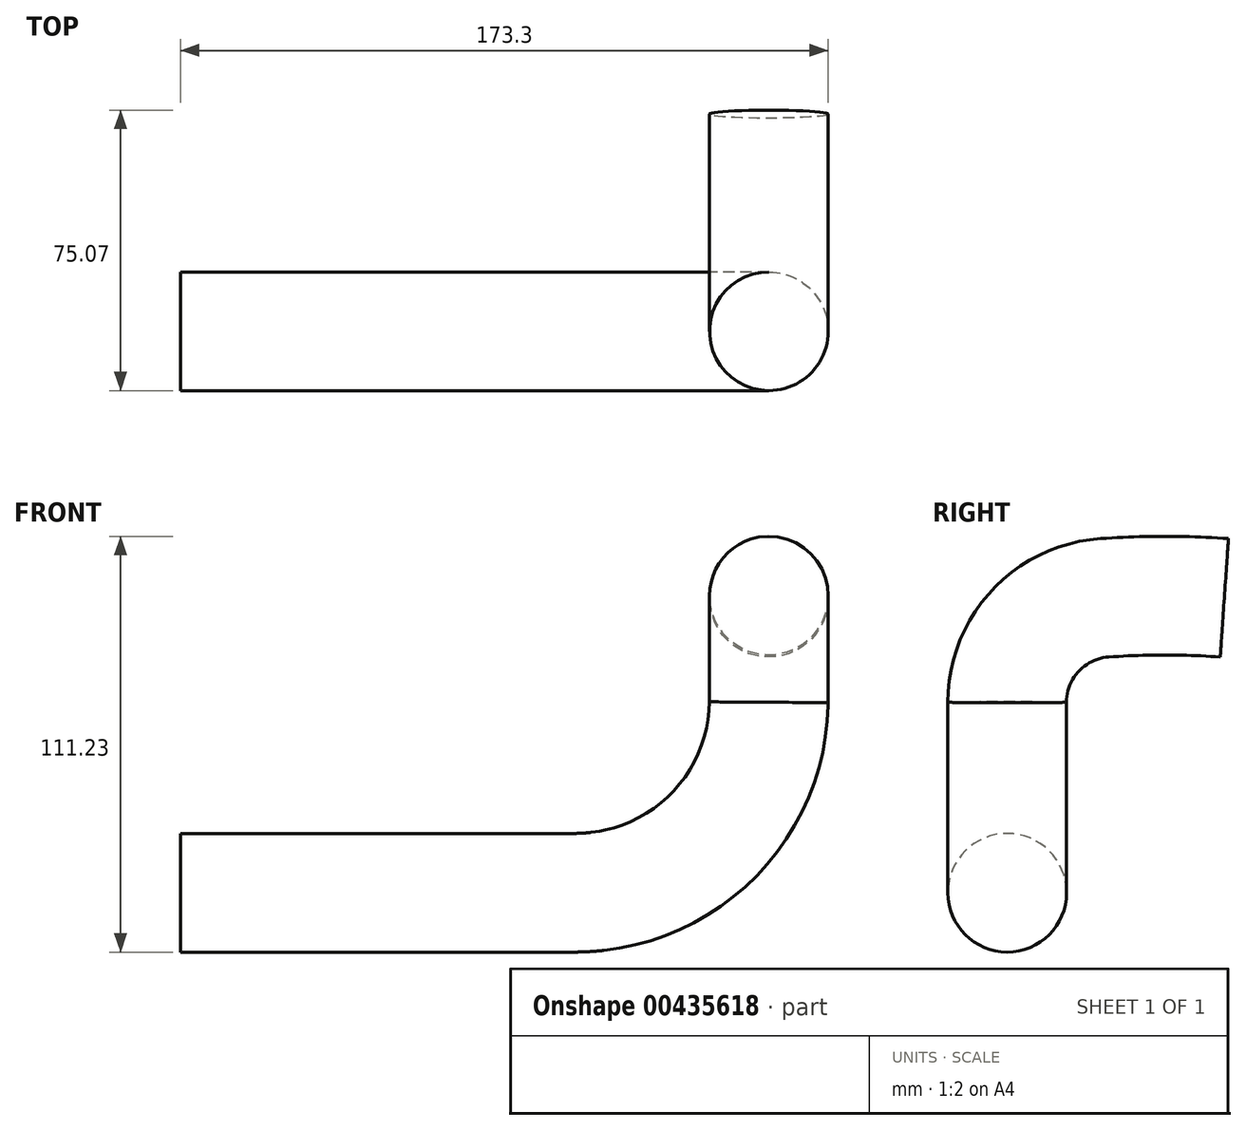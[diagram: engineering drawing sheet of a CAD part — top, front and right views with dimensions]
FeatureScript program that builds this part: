
annotation { "Feature Type Name" : "Feature", "Feature Type Description" : "" }
export const myFeature = defineFeature(function(context is Context, id is Id, definition is map)
    precondition{}
    {
        {
            var Q0;
            Q0=qCreatedBy(makeId("Front.planeOp"),FACE);
            var sketch = newSketch(context, id + "F0", { "sketchPlane" : qUnion([Q0])});
            skLineSegment(sketch, "E0", {"start": v(-80.2, 0) * mm, "end": v(0, 0) * mm});
            skLineSegment(sketch, "E1", {"start": v(0, 0) * mm, "end": v(24.89, 0) * mm});
            skArc(sketch, "E2", {"start": v(24.89, 0) * mm, "mid": v(28.15, 0.1) * mm, "end": v(31.4, 0.36) * mm});
            skArc(sketch, "E3", {"start": v(31.4, 0.36) * mm, "mid": v(63.9, 17) * mm, "end": v(77.23, 50.97) * mm});
            skSolve(sketch);
        }
        {
            var Q0;
            Q0=sQuery(id+"F0.wireOp",VERTEX,"E3.end");
            var Q1;
            Q1=qCreatedBy(makeId("Right.planeOp"),FACE);
            cPlane(context, id + "F1", {"entities" : qUnion([Q0, Q1]), "cplaneType" : CPlaneType.PLANE_POINT, "offset" : 25.4 * mm, "width" : 152.4 * mm, "height" : 152.4 * mm});
        }
        {
            var Q0;
            Q0=qCreatedBy(id+"F1.planeOp",FACE);
            var sketch = newSketch(context, id + "F2", { "sketchPlane" : qUnion([Q0])});
            skArc(sketch, "E4", {"start": v(26.1, 78.93) * mm, "mid": v(7.54, 70.1) * mm, "end": v(0, 50.97) * mm});
            skArc(sketch, "E5", {"start": v(58.1, 78.93) * mm, "mid": v(42.1, 79.48) * mm, "end": v(26.1, 78.93) * mm});
            skSolve(sketch);
        }
        {
            var Q0;
            Q0=qCreatedBy(makeId("Right.planeOp"),FACE);
            var Q1;
            Q1=sQuery(id+"F0.wireOp",VERTEX,"E0.start");
            cPlane(context, id + "F3", {"entities" : qUnion([Q0, Q1]), "cplaneType" : CPlaneType.PLANE_POINT, "offset" : 25.4 * mm, "oppositeDirection" : true, "width" : 152.4 * mm, "height" : 152.4 * mm});
        }
        {
            var Q0;
            Q0=qCreatedBy(id+"F3.planeOp",FACE);
            var sketch = newSketch(context, id + "F4", { "sketchPlane" : qUnion([Q0])});
            skCircle(sketch, "E6", {"center": v(0, 0) * mm, "radius": 15.88 * mm});
            skSolve(sketch);
        }
        {
            var Q0;
            Q0=makeQuery(id+"F4.imprint","IMPRINT",FACE,{"disambiguationData":[TD([[makeQuery(id+"F4.imprint","IMPRINT",EDGE,{"derivedFrom":sQuery(id+"F4.wireOp",EDGE,"E6")}),1.0]])]});
            var Q1;
            Q1=sQuery(id+"F0.wireOp",EDGE,"E0");
            var Q2;
            Q2=sQuery(id+"F0.wireOp",EDGE,"E1");
            var Q3;
            Q3=sQuery(id+"F0.wireOp",EDGE,"E2");
            var Q4;
            Q4=sQuery(id+"F0.wireOp",EDGE,"E3");
            var Q5;
            Q5=sQuery(id+"F2.wireOp",EDGE,"E4");
            var Q6;
            Q6=sQuery(id+"F2.wireOp",EDGE,"E5");
            sweep(context, id + "F5", {"profiles" : qUnion([Q0]), "path" : qUnion([Q1, Q2, Q3, Q4, Q5, Q6])});
        }
    });
